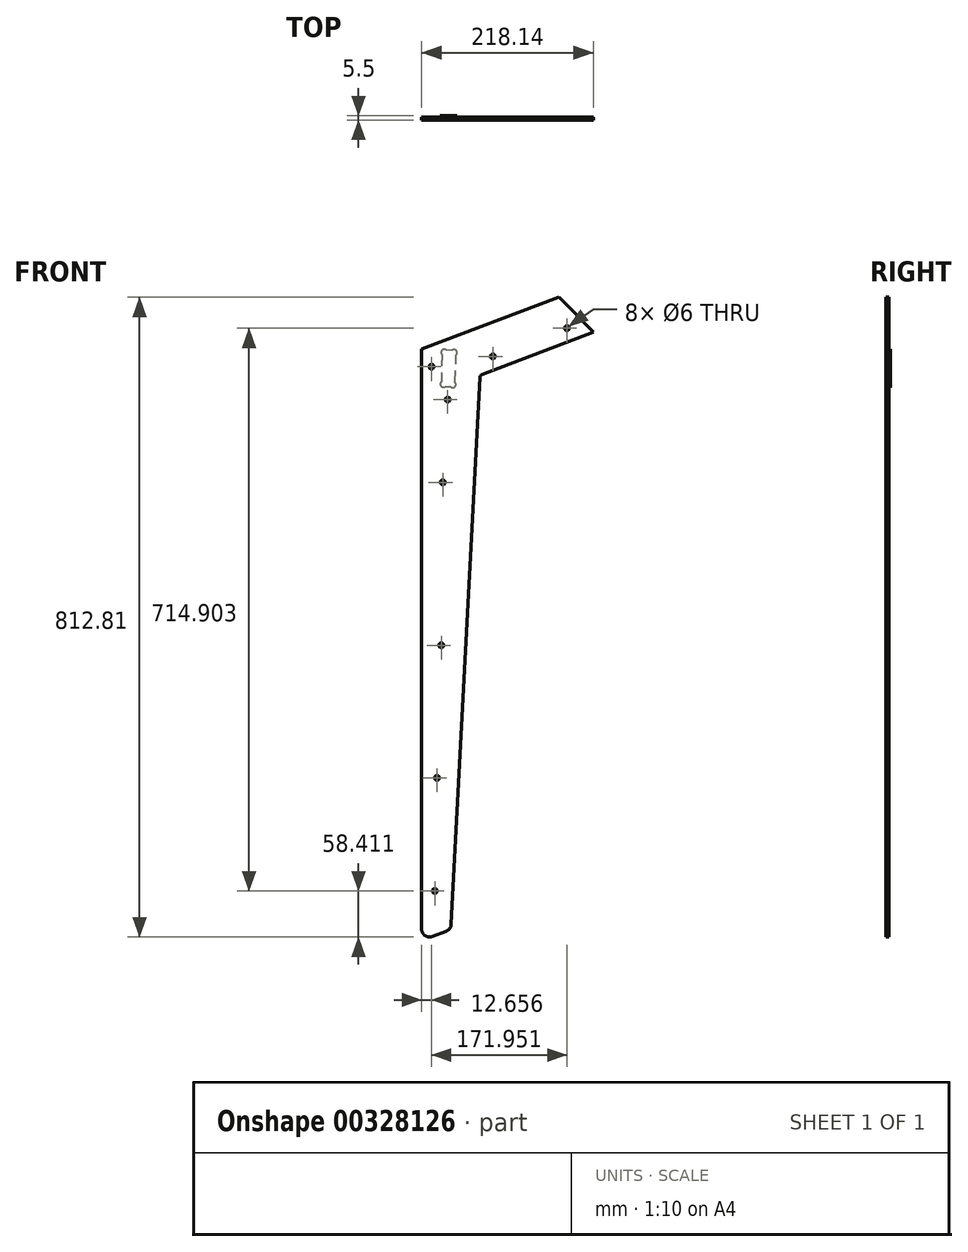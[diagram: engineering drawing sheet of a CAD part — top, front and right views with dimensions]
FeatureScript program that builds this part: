
annotation { "Feature Type Name" : "Feature", "Feature Type Description" : "" }
export const myFeature = defineFeature(function(context is Context, id is Id, definition is map)
    precondition{}
    {
        {
            var Q0;
            Q0=qCreatedBy(makeId("Front.planeOp"),FACE);
            var sketch = newSketch(context, id + "F0", { "sketchPlane" : qUnion([Q0])});
            skLineSegment(sketch, "E0", {"start": v(-101.67, -441.55) * mm, "end": v(-119.33, -448.26) * mm});
            skArc(sketch, "E1", {"start": v(-119.33, -448.26) * mm, "mid": v(-128.56, -447.15) * mm, "end": v(-132.88, -438.91) * mm});
            skLineSegment(sketch, "E2", {"start": v(-132.88, -438.91) * mm, "end": v(-132.88, 297.64) * mm});
            skLineSegment(sketch, "E3", {"start": v(-132.88, 297.64) * mm, "end": v(41.34, 363.9) * mm});
            skLineSegment(sketch, "E4", {"start": v(41.34, 363.9) * mm, "end": v(85.26, 319.44) * mm});
            skLineSegment(sketch, "E5", {"start": v(85.26, 319.44) * mm, "end": v(-56.25, 265.62) * mm});
            skArc(sketch, "E6", {"start": v(-56.25, 265.62) * mm, "mid": v(-58.06, 264.24) * mm, "end": v(-58.82, 262.09) * mm});
            skLineSegment(sketch, "E7", {"start": v(-58.82, 262.09) * mm, "end": v(-95.24, -432.72) * mm});
            skArc(sketch, "E8", {"start": v(-95.24, -432.72) * mm, "mid": v(-97.14, -438.09) * mm, "end": v(-101.67, -441.55) * mm});
            skCircle(sketch, "E9", {"center": v(-99.7, 233.75) * mm, "radius": 3 * mm});
            skCircle(sketch, "E10", {"center": v(-116.14, -390.5) * mm, "radius": 3 * mm});
            skCircle(sketch, "E11", {"center": v(-113.35, -246.7) * mm, "radius": 3 * mm});
            skCircle(sketch, "E12", {"center": v(51.73, 324.4) * mm, "radius": 3 * mm});
            skCircle(sketch, "E13", {"center": v(-120.22, 275.49) * mm, "radius": 3 * mm});
            skCircle(sketch, "E14", {"center": v(-107.92, -78.38) * mm, "radius": 3 * mm});
            skCircle(sketch, "E15", {"center": v(-105.95, 128.63) * mm, "radius": 3 * mm});
            skCircle(sketch, "E16", {"center": v(-42.35, 288.62) * mm, "radius": 3 * mm});
            skArc(sketch, "E17", {"start": v(-96.2, 250.25) * mm, "mid": v(-90.55, 250.06) * mm, "end": v(-90.38, 255.72) * mm});
            skLineSegment(sketch, "E18", {"start": v(-90.38, 255.72) * mm, "end": v(-89.01, 290.34) * mm});
            skArc(sketch, "E19", {"start": v(-89.01, 290.34) * mm, "mid": v(-88.79, 296) * mm, "end": v(-94.45, 296.2) * mm});
            skLineSegment(sketch, "E20", {"start": v(-94.45, 296.2) * mm, "end": v(-101.13, 296.44) * mm});
            skArc(sketch, "E21", {"start": v(-101.13, 296.44) * mm, "mid": v(-106.75, 296.66) * mm, "end": v(-107.03, 291.04) * mm});
            skLineSegment(sketch, "E22", {"start": v(-107.03, 291.04) * mm, "end": v(-107.9, 256.34) * mm});
            skArc(sketch, "E23", {"start": v(-107.9, 256.34) * mm, "mid": v(-108.16, 250.67) * mm, "end": v(-102.49, 250.46) * mm});
            skLineSegment(sketch, "E24", {"start": v(-102.49, 250.46) * mm, "end": v(-96.2, 250.25) * mm});
            skSolve(sketch);
        }
        {
            var Q0;
            Q0=makeQuery(id+"F0.imprint","IMPRINT",FACE,{"disambiguationData":[TD([[makeQuery(id+"F0.imprint","IMPRINT",EDGE,{"derivedFrom":sQuery(id+"F0.wireOp",EDGE,"E0")}),-1.0]])]});
            var Q1;
            Q1=makeQuery(id+"F0.imprint","IMPRINT",FACE,{"disambiguationData":[TD([[makeQuery(id+"F0.imprint","IMPRINT",EDGE,{"derivedFrom":sQuery(id+"F0.wireOp",EDGE,"E10")}),-1.0]])]});
            var Q2;
            Q2=makeQuery(id+"F0.imprint","IMPRINT",FACE,{"disambiguationData":[TD([[makeQuery(id+"F0.imprint","IMPRINT",EDGE,{"derivedFrom":sQuery(id+"F0.wireOp",EDGE,"E11")}),-1.0]])]});
            var Q3;
            Q3=makeQuery(id+"F0.imprint","IMPRINT",FACE,{"disambiguationData":[TD([[makeQuery(id+"F0.imprint","IMPRINT",EDGE,{"derivedFrom":sQuery(id+"F0.wireOp",EDGE,"E14")}),-1.0]])]});
            var Q4;
            Q4=makeQuery(id+"F0.imprint","IMPRINT",FACE,{"disambiguationData":[TD([[makeQuery(id+"F0.imprint","IMPRINT",EDGE,{"derivedFrom":sQuery(id+"F0.wireOp",EDGE,"E15")}),-1.0]])]});
            var Q5;
            Q5=makeQuery(id+"F0.imprint","IMPRINT",FACE,{"disambiguationData":[TD([[makeQuery(id+"F0.imprint","IMPRINT",EDGE,{"derivedFrom":sQuery(id+"F0.wireOp",EDGE,"E13")}),-1.0]])]});
            var Q6;
            Q6=makeQuery(id+"F0.imprint","IMPRINT",FACE,{"disambiguationData":[TD([[makeQuery(id+"F0.imprint","IMPRINT",EDGE,{"derivedFrom":sQuery(id+"F0.wireOp",EDGE,"E9")}),-1.0]])]});
            var Q7;
            Q7=makeQuery(id+"F0.imprint","IMPRINT",FACE,{"disambiguationData":[TD([[makeQuery(id+"F0.imprint","IMPRINT",EDGE,{"derivedFrom":sQuery(id+"F0.wireOp",EDGE,"E16")}),-1.0]])]});
            var Q8;
            Q8=makeQuery(id+"F0.imprint","IMPRINT",FACE,{"disambiguationData":[TD([[makeQuery(id+"F0.imprint","IMPRINT",EDGE,{"derivedFrom":sQuery(id+"F0.wireOp",EDGE,"E12")}),-1.0]])]});
            var Q9;
            Q9=makeQuery(id+"F0.imprint","IMPRINT",FACE,{"disambiguationData":[TD([[makeQuery(id+"F0.imprint","IMPRINT",EDGE,{"derivedFrom":sQuery(id+"F0.wireOp",EDGE,"E17")}),1.0]])]});
            extrude(context, id + "F1", {"entities" : qUnion([Q0, Q1, Q2, Q3, Q4, Q5, Q6, Q7, Q8, Q9]), "depth" : 18 * mm});
        }
        {
            var Q0;
            Q0=makeQuery(id+"F0.imprint","IMPRINT",FACE,{"disambiguationData":[TD([[makeQuery(id+"F0.imprint","IMPRINT",EDGE,{"derivedFrom":sQuery(id+"F0.wireOp",EDGE,"E10")}),-1.0]])]});
            var Q1;
            Q1=makeQuery(id+"F0.imprint","IMPRINT",FACE,{"disambiguationData":[TD([[makeQuery(id+"F0.imprint","IMPRINT",EDGE,{"derivedFrom":sQuery(id+"F0.wireOp",EDGE,"E11")}),-1.0]])]});
            var Q2;
            Q2=makeQuery(id+"F0.imprint","IMPRINT",FACE,{"disambiguationData":[TD([[makeQuery(id+"F0.imprint","IMPRINT",EDGE,{"derivedFrom":sQuery(id+"F0.wireOp",EDGE,"E14")}),-1.0]])]});
            var Q3;
            Q3=makeQuery(id+"F0.imprint","IMPRINT",FACE,{"disambiguationData":[TD([[makeQuery(id+"F0.imprint","IMPRINT",EDGE,{"derivedFrom":sQuery(id+"F0.wireOp",EDGE,"E15")}),-1.0]])]});
            var Q4;
            Q4=makeQuery(id+"F0.imprint","IMPRINT",FACE,{"disambiguationData":[TD([[makeQuery(id+"F0.imprint","IMPRINT",EDGE,{"derivedFrom":sQuery(id+"F0.wireOp",EDGE,"E13")}),-1.0]])]});
            var Q5;
            Q5=makeQuery(id+"F0.imprint","IMPRINT",FACE,{"disambiguationData":[TD([[makeQuery(id+"F0.imprint","IMPRINT",EDGE,{"derivedFrom":sQuery(id+"F0.wireOp",EDGE,"E9")}),-1.0]])]});
            var Q6;
            Q6=makeQuery(id+"F0.imprint","IMPRINT",FACE,{"disambiguationData":[TD([[makeQuery(id+"F0.imprint","IMPRINT",EDGE,{"derivedFrom":sQuery(id+"F0.wireOp",EDGE,"E16")}),-1.0]])]});
            var Q7;
            Q7=makeQuery(id+"F0.imprint","IMPRINT",FACE,{"disambiguationData":[TD([[makeQuery(id+"F0.imprint","IMPRINT",EDGE,{"derivedFrom":sQuery(id+"F0.wireOp",EDGE,"E12")}),-1.0]])]});
            extrude(context, id + "F2", {"entities" : qUnion([Q0, Q1, Q2, Q3, Q4, Q5, Q6, Q7]), "operationType" : NewBodyOperationType.REMOVE, "depth" : 14 * mm});
        }
        {
            var Q0;
            Q0=makeQuery(id+"F0.imprint","IMPRINT",FACE,{"disambiguationData":[TD([[makeQuery(id+"F0.imprint","IMPRINT",EDGE,{"derivedFrom":sQuery(id+"F0.wireOp",EDGE,"E17")}),1.0]])]});
            extrude(context, id + "F3", {"entities" : qUnion([Q0]), "operationType" : NewBodyOperationType.REMOVE, "depth" : 12.5 * mm});
        }
    });
